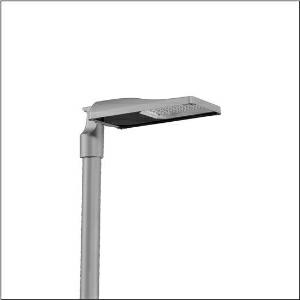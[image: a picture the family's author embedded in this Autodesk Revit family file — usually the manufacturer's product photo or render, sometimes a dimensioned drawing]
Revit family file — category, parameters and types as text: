
# Revit family: streetlight_sl_31_mini___st1_0a_5xh6d3ab08ga_4fba
name_source: partatom
category: Lighting Fixtures
units: mm (PartAtom-declared; Revit-internal decimal feet)

## family parameters
Cut with Voids When Loaded = No
Host = Face
Light Source = No
Part Type = Normal
Room Calculation Point = No
Round Connector Dimension = Use Diameter
Shared = No

## types (1)
- --- (1 x LED, 5710 lm, 37.3 W, 3000K)
    Apparent Load = 37 VA
    CIE Flux Codes = 37 72 97 100 100
    Color Rendering = 70
    Color Temperature = 3000K
    Default Elevation = 1800 mm
    Description = Streetlight SL 31 mini Easy LST mast luminaire for post-top, side-entry; light control with lens of PMMA; light distribution: ST1.0a, direct asymmetric distribution, for standard-compliant lighting for roads and squares; LED: luminous flux: 5.710lm, light colour: 730, colour temperature: 3000K; luminous efficacy: 153,1lm/W; control: pre-setting: linear dimming characteristic, flexible luminous flux parameterisation, time-dependent luminous flux control, constant luminous flux control, power reduction, intelligent temperature release in ECG and LED module, overheat protection; luminaire housing, of diecast aluminium, Siteco® metallic grey (DB 702S), corrosivity category C5 high according to DIN EN ISO 12944; cover of toughened safety glass, transparent, opened without tools; mast flange of diecast aluminium, Siteco® metallic grey (DB 702S), spigot size: 76/60mm, mast flange included unmounted; with cable H07RN-F 3x 1.5mm², cable length: 6,5m, connection cable pre-assembled; mains connection: 220..240V, AC, 50/60Hz; power consumption (at start of service life): 37,3W / (at end of service life): 38,7W / (with reduced operation 50%): 17,5W; protection rating (complete): IP66; insulation class (complete): insulation class II (safety insulation); impact resistance: IK09; certification: CE, ENEC, ENEC+, VDE, UKCA; permissible operating ambient temperature for outdoor applications: -40..+50°C; packaging unit: 1 piece

Light Distribution: ST1.0a
    Height = 76 mm
    Lamp = 1 x LED
    Lamp Light Flux = 5710 lm
    Lamp Power = 37.3 W
    Lamp count = 1
    Length = 547 mm
    Luminous efficacy = 153 lm/W
    Manufacturer = Siteco
    ModVariant = No
    Model = 5XH6D3AB08GA
    Number of Poles = 1
    OnlyDefault = Yes
    Power Factor = 1
    Product Name = Streetlight SL 31 mini | ST1.0a
    Product group = mast luminaire | pylon top
    ProductGroupID = 6100
    Protection Class = Protection class II
    Protection Degree = IP 66
    RLX_Detail_Level = 1
    RLX_Emergency_Light_Flux = 0 lm
    RLX_Emergency_Type = 0
    RLX_Emergency_Type_DB = No
    RlxData = <blob elided: 39605 chars, md5=19206b4e>
    Socket = socket
    Standby Power = 0 W
    System Light Flux = 5710 lm
    System Power = 37 W
    Type Comments = factory setting: luminous flux: 100 % | dim-lin: 254 | 386 mA
    Type Image = l_1300326.jpg
    URL = http://relux.com
    VarID = @adj_051120
    Voltage = 0 V
    Weight = 0.00 kg
    Width = 265 mm

## geometry (parser evidence)
native form markers: Blend x4, Sweep x10
no freeform markers — native parametric forms only
